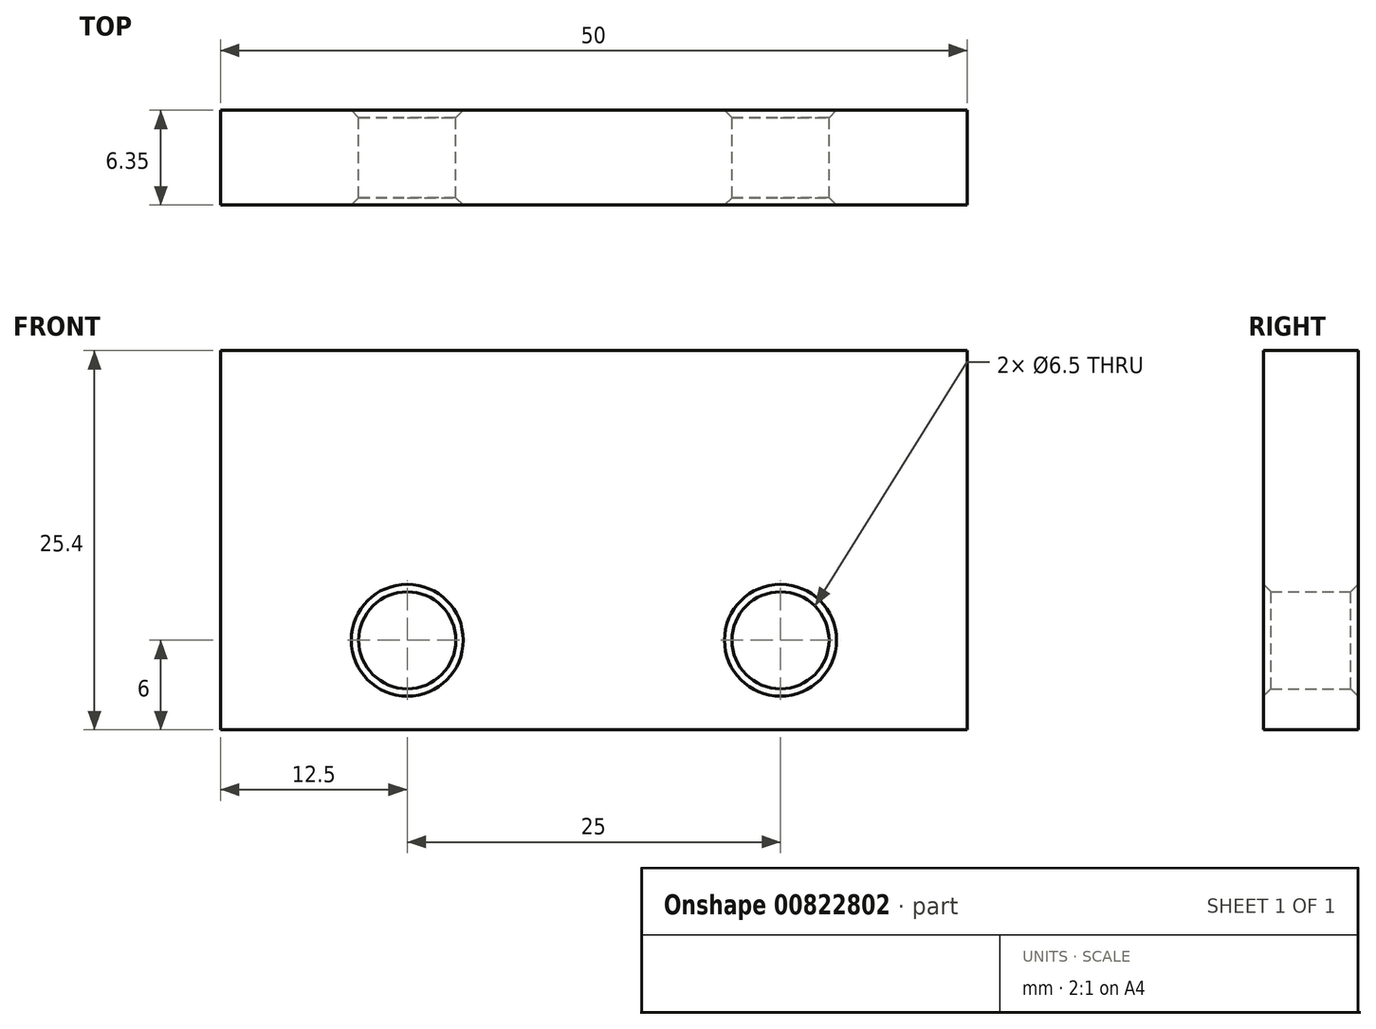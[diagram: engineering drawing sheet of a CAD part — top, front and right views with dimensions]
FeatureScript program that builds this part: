
annotation { "Feature Type Name" : "Feature", "Feature Type Description" : "" }
export const myFeature = defineFeature(function(context is Context, id is Id, definition is map)
    precondition{}
    {
        {
            var Q0;
            Q0=qCreatedBy(makeId("Front.planeOp"),FACE);
            var sketch = newSketch(context, id + "F0", { "sketchPlane" : qUnion([Q0])});
            skLineSegment(sketch, "E0.bottom", {"start": v(25, 12.7) * mm, "end": v(-25, 12.7) * mm});
            skLineSegment(sketch, "E0.top", {"start": v(25, -12.7) * mm, "end": v(-25, -12.7) * mm});
            skLineSegment(sketch, "E0.left", {"start": v(25, 12.7) * mm, "end": v(25, -12.7) * mm});
            skLineSegment(sketch, "E0.right", {"start": v(-25, 12.7) * mm, "end": v(-25, -12.7) * mm});
            skPoint(sketch, "E0.middle", {"position": v(0, 0) * mm});
            skLineSegment(sketch, "E1", {"start": v(0, 0) * mm, "end": v(0, -18.92) * mm, "construction": true});
            skLineSegment(sketch, "E2", {"start": v(-12.5, -6.7) * mm, "end": v(0, -6.7) * mm, "construction": true});
            skCircle(sketch, "E3", {"center": v(-12.5, -6.7) * mm, "radius": 3.25 * mm});
            skCircle(sketch, "E4.MirrorC", {"center": v(12.5, -6.7) * mm, "radius": 3.25 * mm});
            skSolve(sketch);
        }
        {
            var Q0;
            Q0 = qSketchRegion(id + "F0", true);
            extrude(context, id + "F1", {"entities" : qUnion([Q0]), "depth" : 6.35 * mm, "offsetDistance" : 25 * mm});
        }
        {
            var Q0;
            Q0=makeQuery(id+"F1.opExtrude","SWEPT_FACE",FACE,{"disambiguationData":[OSD([sQuery(id+"F0.wireOp",EDGE,"E3")])]});
            var Q1;
            Q1=makeQuery(id+"F1.opExtrude","SWEPT_FACE",FACE,{"disambiguationData":[OSD([sQuery(id+"F0.wireOp",EDGE,"E4.MirrorC")])]});
            chamfer(context, id + "F2", {"entities" : qUnion([Q0, Q1]), "width" : 0.5 * mm, "tangentPropagation" : true});
        }
    });
